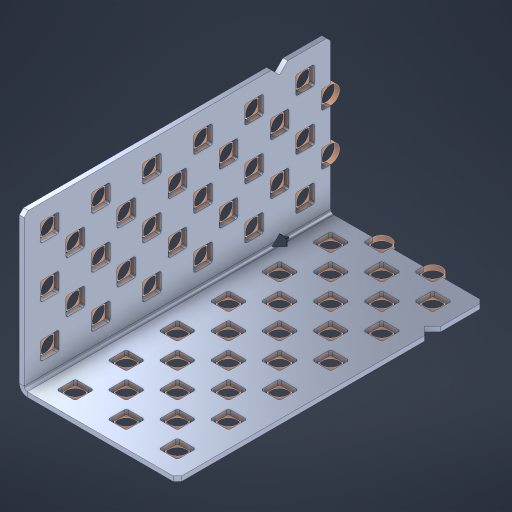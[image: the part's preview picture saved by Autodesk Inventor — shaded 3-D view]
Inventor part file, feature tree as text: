
AUTODESK INVENTOR PART (.ipt)
format: ipt  version: 2023 (Build 270158000, 158)  size: 968,704 bytes
history: native  units: in
note: dims shown in document units (in); Inventor stores cm internally (conversion verified against a paired STEP export)
features: other x66, extrude x58, sheet_metal_op x8, sketch x7, pattern_linear x3, mirror x1, chamfer x1
ambient origin geometry x8: Origin, YZ Plane, XZ Plane, XY Plane, X Axis, Y Axis, Z Axis, Center Point
bodies: Solid1 (feature_tree), Body (feature_tree)
feature tree (144):
  sheet_metal_op  "Flanges"
  sheet_metal_op  "Body Pattern"
  pattern_linear  "Center Double"  Spacing1=1.5in  [1 undecoded]
  pattern_linear  "Center Pattern"  Spacing1=0.1875in  [1 undecoded]
  other  "Arc Length"
  pattern_linear  "Notch Pattern"  Spacing1=0.0469in  [1 undecoded]
  other  "Diagonal Plane"
  mirror  "Everything Mirrored"
  chamfer  "End Chamfer"
  sketch  "Sketch1"  dims[d0=1.5in]
  other  "Plate1"
  sketch  "Sketch2"  dims[d1=3.0in]
  other  "Plate2"
  sheet_metal_op  "Bend1"
  sheet_metal_op  "Corner1"
  sketch  "Sketch8"  dims[d2=0.0469in]
  sketch  "Sketch9"  dims[d3=0.0469in]
  other  "Srf91"
  sheet_metal_op  "Body Pattern Sketch"
  other  "Srf92"
  sketch  "Sketch13"  dims[d4=0.0234in]
  sketch  "Sketch15"  dims[d5=0.0938in]
  sketch  "Sketch16"  dims[d6=0.0469in d7=1.5in d8=90.0deg d9=0.0312in d10=0.1875in d11=0.0469in d12=0.0469in d49=0.182in d50=0.02in d52=0.25in d53=0.0469in d54=0.0in d55=0.172in d56=1.0in d57=0.0in d85=0.1473in d86=0.1659in d89=0.0469in d90=0.0in d91=0.04in d92=0.0491in d95=2.5in d96=0.04in d97=0.25in d98=45.0deg d106=0.182in d107=0.02in d110=0.0469in d111=0.0in d112=0.172in d113=0.5in d114=0.0in d117=0.5in d126=0.0491in d127=0.1227in d128=0.08in d129=0.04in d130=2.5in d131=0.25in d132=2.3622in d134=0.5in d135=1.1811in d137=0.5in d140=0.5in d141=1.0in d142=0.3937in d144=0.5in d145=0.071in d146=0.7874in d148=0.5in]
  other  "Srf786"
  other  "Srf856"
  other  "Srf889"
  other  "Srf890"
  other  "Srf891"
  other  "Srf1275"
  other  "Srf1276"
  other  "Srf1278"
  other  "Srf1277"
  other  "Srf1285"
  other  "Srf1286"
  other  "Srf1287"
  other  "Srf1445"
  other  "Srf1446"
  other  "Srf1537"
  other  "Srf1538"
  other  "Srf2009"
  other  "Srf2010"
  other  "Srf2011"
  other  "Srf2012"
  other  "Srf2013"
  other  "Srf2014"
  other  "Srf2043"
  other  "Srf2044"
  other  "Srf2045"
  other  "Srf2046"
  other  "Srf2047"
  other  "Srf2076"
  other  "Srf2077"
  other  "Srf2078"
  other  "Srf2079"
  other  "Srf2080"
  other  "Srf2081"
  other  "Srf2082"
  other  "Srf2083"
  other  "Srf2084"
  other  "Srf2085"
  other  "Srf2086"
  other  "Srf2087"
  other  "Srf2088"
  other  "Srf2089"
  other  "Srf2090"
  other  "Srf2091"
  other  "Srf2179"
  other  "Srf2180"
  other  "Srf2181"
  other  "Srf2182"
  other  "Srf2183"
  other  "Srf2184"
  other  "Srf2185"
  other  "Srf2186"
  other  "Srf2187"
  other  "Srf2188"
  other  "Srf2189"
  other  "Srf2190"
  other  "Srf2191"
  other  "Srf2192"
  other  "Srf2193"
  sheet_metal_op  "Body Stamp"
  sheet_metal_op  "Body Circle"
  other  "Center Stamp"
  other  "Center Circle"
  sheet_metal_op  "Notch"
  extrude  "ExtrusionSrf92"  Depth=0.0469in
  extrude  "ExtrusionSrf856"  Depth=0.182in
  extrude  "ExtrusionSrf889"  Depth=0.02in
  extrude  "ExtrusionSrf890"  Depth=0.25in
  extrude  "ExtrusionSrf891"  Depth=0.0469in
  extrude  "ExtrusionSrf1275"  TaperAngle=0.0deg  [1 undecoded]
  extrude  "ExtrusionSrf1276"  Depth=0.5in
  extrude  "ExtrusionSrf1277"  Depth=0.5in TaperAngle=0.0deg
  extrude  "ExtrusionSrf1345"  Depth=0.5in
  extrude  "ExtrusionSrf1346"  Depth=0.5in
  extrude  "ExtrusionSrf1347"  Depth=0.0469in
  extrude  "ExtrusionSrf1348"  Depth=0.5in TaperAngle=0.0deg
  extrude  "ExtrusionSrf1445"  Depth=0.5in
  extrude  "ExtrusionSrf1446"  Depth=0.25in TaperAngle=45.0deg
  extrude  "ExtrusionSrf1537"  Depth=0.182in
  extrude  "ExtrusionSrf1538"  Depth=0.02in
  extrude  "ExtrusionSrf2009"  Depth=0.0469in
  extrude  "ExtrusionSrf2010"  TaperAngle=0.0deg  [1 undecoded]
  extrude  "ExtrusionSrf2011"  Depth=0.5in
  extrude  "ExtrusionSrf2012"  Depth=0.5in TaperAngle=0.0deg
  extrude  "ExtrusionSrf2013"  Depth=0.5in
  extrude  "ExtrusionSrf2014"  Depth=0.5in
  extrude  "ExtrusionSrf2043"  Depth=0.5in
  extrude  "ExtrusionSrf2044"  Depth=0.5in
  extrude  "ExtrusionSrf2045"  Depth=0.5in
  extrude  "ExtrusionSrf2046"  Depth=0.5in
  extrude  "ExtrusionSrf2047"  Depth=0.25in
  extrude  "ExtrusionSrf2076"  Depth=0.5in
  extrude  "ExtrusionSrf2077"  Depth=0.5in
  extrude  "ExtrusionSrf2078"  Depth=0.5in
  extrude  "ExtrusionSrf2079"  Depth=0.5in
  extrude  "ExtrusionSrf2080"  Depth=0.3937in
  extrude  "ExtrusionSrf2081"  Depth=0.5in
  extrude  "ExtrusionSrf2082"  Depth=0.5in
  extrude  "ExtrusionSrf2083"  [1 undecoded]
  extrude  "ExtrusionSrf2084"  [1 undecoded]
  extrude  "ExtrusionSrf2085"  [1 undecoded]
  extrude  "ExtrusionSrf2086"  [1 undecoded]
  extrude  "ExtrusionSrf2087"  [1 undecoded]
  extrude  "ExtrusionSrf2088"  [1 undecoded]
  extrude  "ExtrusionSrf2089"  [1 undecoded]
  extrude  "ExtrusionSrf2090"  [1 undecoded]
  extrude  "ExtrusionSrf2091"  [1 undecoded]
  extrude  "ExtrusionSrf2179"  [1 undecoded]
  extrude  "ExtrusionSrf2180"  [1 undecoded]
  extrude  "ExtrusionSrf2181"  [1 undecoded]
  extrude  "ExtrusionSrf2182"  [1 undecoded]
  extrude  "ExtrusionSrf2183"  [1 undecoded]
  extrude  "ExtrusionSrf2184"  [1 undecoded]
  extrude  "ExtrusionSrf2185"  [1 undecoded]
  extrude  "ExtrusionSrf2186"  [1 undecoded]
  extrude  "ExtrusionSrf2187"  [1 undecoded]
  extrude  "ExtrusionSrf2188"  [1 undecoded]
  extrude  "ExtrusionSrf2189"  [1 undecoded]
  extrude  "ExtrusionSrf2190"  [1 undecoded]
  extrude  "ExtrusionSrf2191"  [1 undecoded]
  extrude  "ExtrusionSrf2192"  [1 undecoded]
  extrude  "ExtrusionSrf2193"  [1 undecoded]
note: 29 required parameter values undecoded (feature->parameter linkage not recoverable at this tier; creation-order binding heuristic only, values carry confidence <= 0.55)
